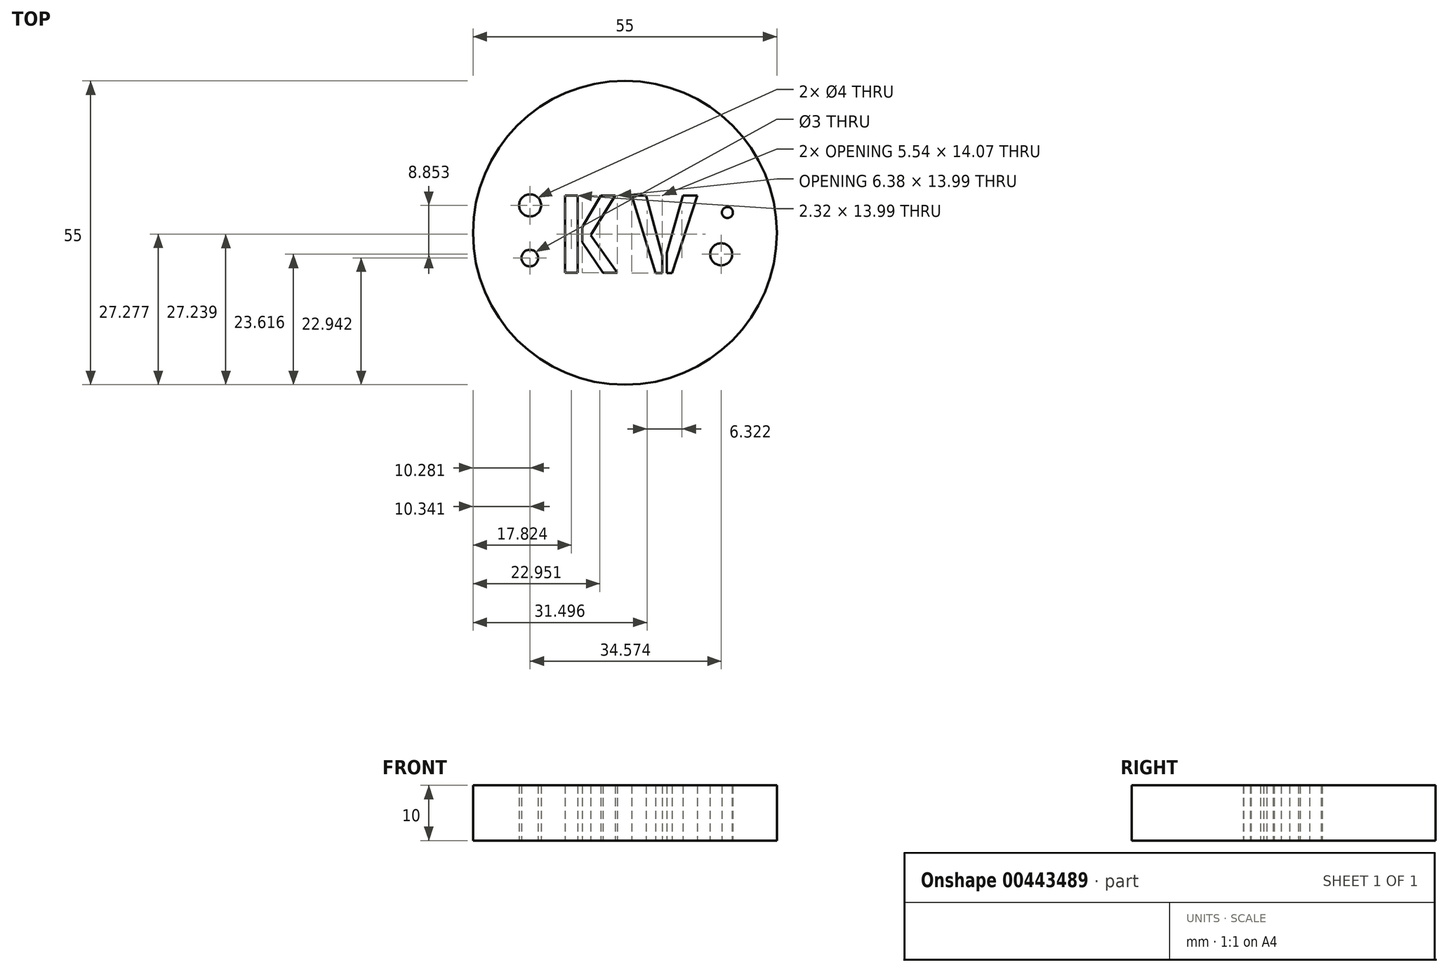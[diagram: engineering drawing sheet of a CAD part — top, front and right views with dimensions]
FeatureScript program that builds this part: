
annotation { "Feature Type Name" : "Feature", "Feature Type Description" : "" }
export const myFeature = defineFeature(function(context is Context, id is Id, definition is map)
    precondition{}
    {
        {
            var Q0;
            Q0=qCreatedBy(makeId("Top.planeOp"),FACE);
            var sketch = newSketch(context, id + "F0", { "sketchPlane" : qUnion([Q0])});
            skCircle(sketch, "E0", {"center": v(0, 0) * mm, "radius": 22.5 * mm});
            skCircle(sketch, "E1", {"center": v(0, 0) * mm, "radius": 27.5 * mm});
            skText(sketch, "E2", { "text": "KV", "fontName": "AllertaStencil-Regular.ttf"});
            skCircle(sketch, "E3", {"center": v(-17.22, -4.56) * mm, "radius": 1.5 * mm});
            skCircle(sketch, "E4", {"center": v(-17.16, 4.97) * mm, "radius": 2 * mm});
            skCircle(sketch, "E5", {"center": v(18.54, 3.68) * mm, "radius": 1 * mm});
            skCircle(sketch, "E6", {"center": v(17.42, -3.88) * mm, "radius": 2 * mm});
            const initialGuessF0  = {"E2": [-0.0126, -0.00722, 1, 0, 0.014]};
            skSetInitialGuess(sketch, initialGuessF0);
            skSolve(sketch);
        }
        {
            var Q0;
            Q0=makeQuery(id+"F0.imprint","IMPRINT",FACE,{"disambiguationData":[TD([[makeQuery(id+"F0.imprint","IMPRINT",EDGE,{"derivedFrom":sQuery(id+"F0.wireOp",EDGE,"E0")}),1.0]])]});
            var Q1;
            Q1=makeQuery(id+"F0.imprint","IMPRINT",FACE,{"disambiguationData":[TD([[makeQuery(id+"F0.imprint","IMPRINT",EDGE,{"derivedFrom":sQuery(id+"F0.wireOp",EDGE,"E0")}),-1.0]])]});
            extrude(context, id + "F1", {"entities" : qUnion([Q0, Q1]), "depth" : 10 * mm});
        }
    });
